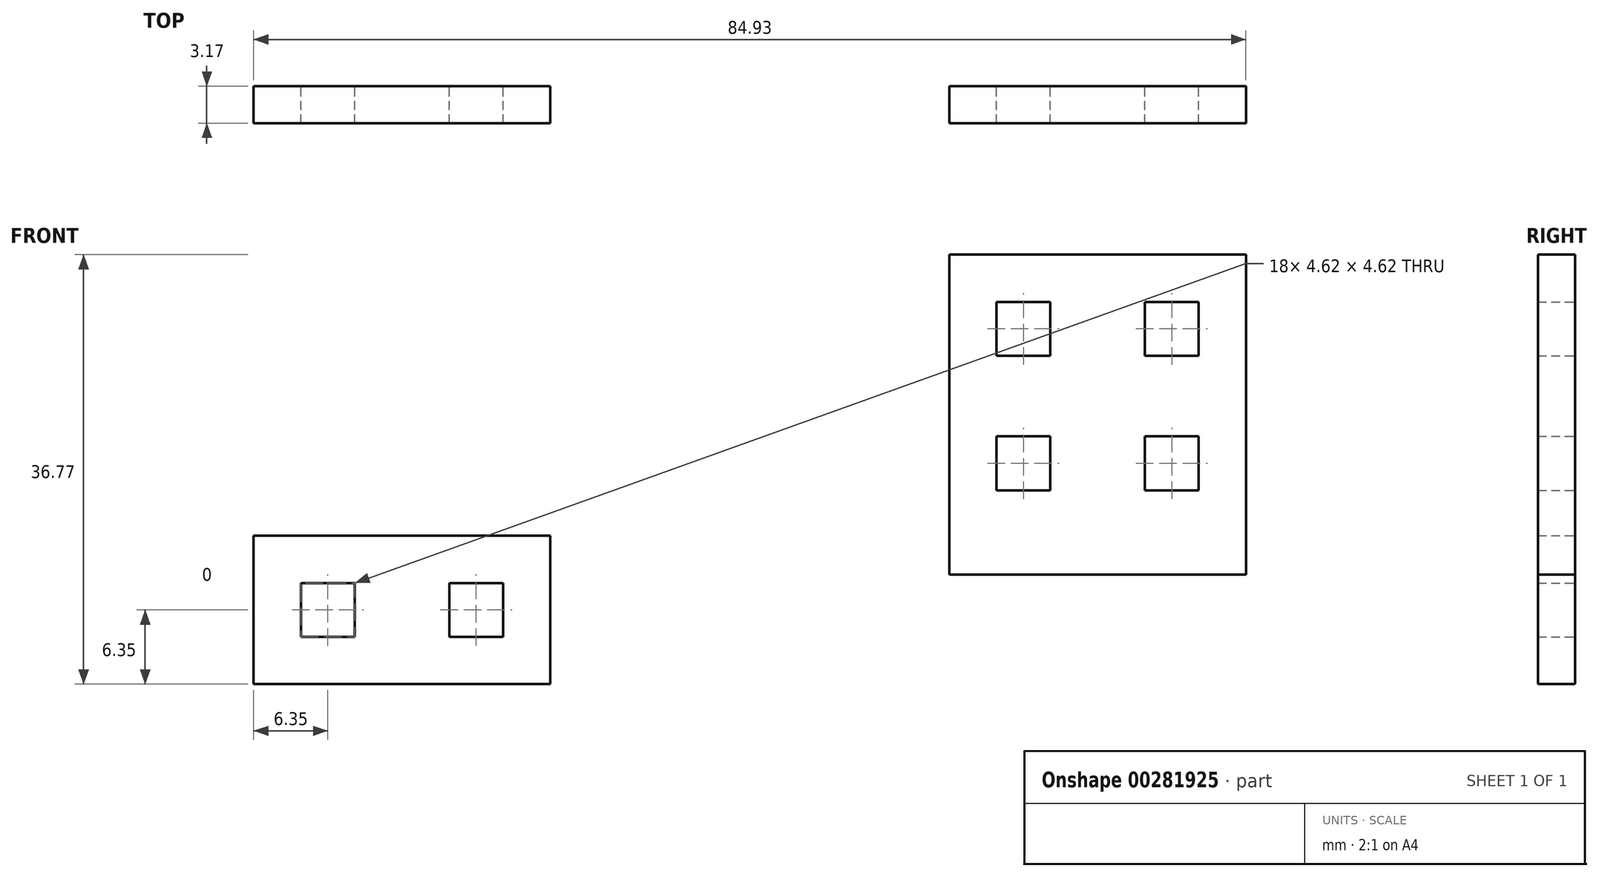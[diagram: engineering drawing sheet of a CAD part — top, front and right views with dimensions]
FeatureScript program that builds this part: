
annotation { "Feature Type Name" : "Feature", "Feature Type Description" : "" }
export const myFeature = defineFeature(function(context is Context, id is Id, definition is map)
    precondition{}
    {
        {
            var Q0;
            Q0=qCreatedBy(makeId("Front.planeOp"),FACE);
            var sketch = newSketch(context, id + "F0", { "sketchPlane" : qUnion([Q0])});
            skLineSegment(sketch, "E0.top", {"start": v(-12.7, -12.7) * mm, "end": v(12.7, -12.7) * mm});
            skLineSegment(sketch, "E0.left", {"start": v(-12.7, 0) * mm, "end": v(-12.7, -12.7) * mm});
            skLineSegment(sketch, "E0.right", {"start": v(12.7, 0) * mm, "end": v(12.7, -12.7) * mm});
            skLineSegment(sketch, "E1.left", {"start": v(46.83, 24.07) * mm, "end": v(46.83, -13.76) * mm});
            skLineSegment(sketch, "E1.right", {"start": v(72.23, 24.07) * mm, "end": v(72.23, -13.76) * mm});
            skPoint(sketch, "E1.middle", {"position": v(59.53, 11.5) * mm});
            skPoint(sketch, "E2", {"position": v(-8.66, -4.04) * mm});
            skPoint(sketch, "E3", {"position": v(-8.66, -8.66) * mm});
            skLineSegment(sketch, "E4", {"start": v(-8.66, -4.04) * mm, "end": v(-8.66, -8.66) * mm});
            skLineSegment(sketch, "E5", {"start": v(-8.66, -8.66) * mm, "end": v(-4.04, -8.66) * mm});
            skLineSegment(sketch, "E6", {"start": v(-4.04, -8.66) * mm, "end": v(-4.04, -4.04) * mm});
            skLineSegment(sketch, "E7", {"start": v(-4.04, -4.04) * mm, "end": v(-8.66, -4.04) * mm});
            skPoint(sketch, "E8.1.0.1", {"position": v(4.04, -4.04) * mm});
            skPoint(sketch, "E8.1.0.4", {"position": v(4.04, -8.66) * mm});
            skLineSegment(sketch, "E8.1.0.6", {"start": v(8.66, -8.66) * mm, "end": v(8.66, -4.04) * mm});
            skLineSegment(sketch, "E8.1.0.7", {"start": v(4.04, -8.66) * mm, "end": v(8.66, -8.66) * mm});
            skLineSegment(sketch, "E8.1.0.8", {"start": v(4.04, -4.04) * mm, "end": v(4.04, -8.66) * mm});
            skLineSegment(sketch, "E8.1.0.9", {"start": v(8.66, -4.04) * mm, "end": v(4.04, -4.04) * mm});
            skPoint(sketch, "E9", {"position": v(46.83, -11.9) * mm});
            skPoint(sketch, "E10", {"position": v(48.79, -13.76) * mm});
            skPoint(sketch, "E11", {"position": v(74.82, -13.76) * mm});
            skPoint(sketch, "E12", {"position": v(72.23, -11.82) * mm});
            skLineSegment(sketch, "E13.0.1.0", {"start": v(50.87, 20.03) * mm, "end": v(50.87, 15.4) * mm});
            skLineSegment(sketch, "E13.0.1.1", {"start": v(50.87, 15.4) * mm, "end": v(55.5, 15.4) * mm});
            skLineSegment(sketch, "E13.0.1.2", {"start": v(55.5, 20.03) * mm, "end": v(50.87, 20.03) * mm});
            skLineSegment(sketch, "E13.0.1.3", {"start": v(55.5, 15.4) * mm, "end": v(55.5, 20.03) * mm});
            skLineSegment(sketch, "E13.0.2.0", {"start": v(50.87, 8.51) * mm, "end": v(50.87, 3.9) * mm});
            skLineSegment(sketch, "E13.0.2.1", {"start": v(50.87, 3.9) * mm, "end": v(55.5, 3.9) * mm});
            skLineSegment(sketch, "E13.0.2.2", {"start": v(55.5, 8.51) * mm, "end": v(50.87, 8.51) * mm});
            skLineSegment(sketch, "E13.0.2.3", {"start": v(55.5, 3.9) * mm, "end": v(55.5, 8.51) * mm});
            skPoint(sketch, "E14", {"position": v(46.83, 0) * mm});
            skPoint(sketch, "E15", {"position": v(72.23, 0) * mm});
            skPoint(sketch, "E16", {"position": v(50.87, -3.32) * mm});
            skLineSegment(sketch, "E17", {"start": v(46.83, -3.32) * mm, "end": v(72.23, -3.32) * mm});
            skLineSegment(sketch, "E18.1.0.1", {"start": v(63.57, 3.9) * mm, "end": v(68.2, 3.9) * mm});
            skLineSegment(sketch, "E18.1.0.2", {"start": v(68.2, 15.4) * mm, "end": v(68.2, 20.03) * mm});
            skLineSegment(sketch, "E18.1.0.3", {"start": v(63.57, 20.03) * mm, "end": v(63.57, 15.4) * mm});
            skLineSegment(sketch, "E18.1.0.4", {"start": v(63.57, 8.51) * mm, "end": v(63.57, 3.9) * mm});
            skLineSegment(sketch, "E18.1.0.5", {"start": v(68.2, 8.51) * mm, "end": v(63.57, 8.51) * mm});
            skLineSegment(sketch, "E18.1.0.7", {"start": v(68.2, 20.03) * mm, "end": v(63.57, 20.03) * mm});
            skLineSegment(sketch, "E18.1.0.9", {"start": v(68.2, 3.9) * mm, "end": v(68.2, 8.51) * mm});
            skLineSegment(sketch, "E18.1.0.11", {"start": v(63.57, 15.4) * mm, "end": v(68.2, 15.4) * mm});
            skLineSegment(sketch, "E19", {"start": v(12.7, 0) * mm, "end": v(-12.7, 0) * mm});
            skPoint(sketch, "E20.orphan", {"position": v(12.7, 12.7) * mm});
            skPoint(sketch, "E21.orphan", {"position": v(-12.7, 12.7) * mm});
            skPoint(sketch, "E22", {"position": v(72.23, 20.03) * mm});
            skPoint(sketch, "E23", {"position": v(72.23, 24.07) * mm});
            skLineSegment(sketch, "E24", {"start": v(72.23, 24.07) * mm, "end": v(46.83, 24.07) * mm});
            skPoint(sketch, "E25.orphan", {"position": v(72.23, 36.77) * mm});
            skPoint(sketch, "E26.orphan", {"position": v(46.83, 36.77) * mm});
            skSolve(sketch);
        }
        {
            var Q0;
            Q0=makeQuery(id+"F0.imprint","IMPRINT",FACE,{"disambiguationData":[TD([[makeQuery(id+"F0.imprint","IMPRINT",EDGE,{"derivedFrom":sQuery(id+"F0.wireOp",EDGE,"E0.top")}),1.0]])]});
            var Q1;
            Q1=makeQuery(id+"F0.imprint","IMPRINT",FACE,{"disambiguationData":[TD([[makeQuery(id+"F0.imprint","IMPRINT",EDGE,{"derivedFrom":sQuery(id+"F0.wireOp",EDGE,"E13.0.1.0")}),-1.0]])]});
            extrude(context, id + "F1", {"entities" : qUnion([Q0, Q1]), "depth" : 3.17 * mm});
        }
    });
